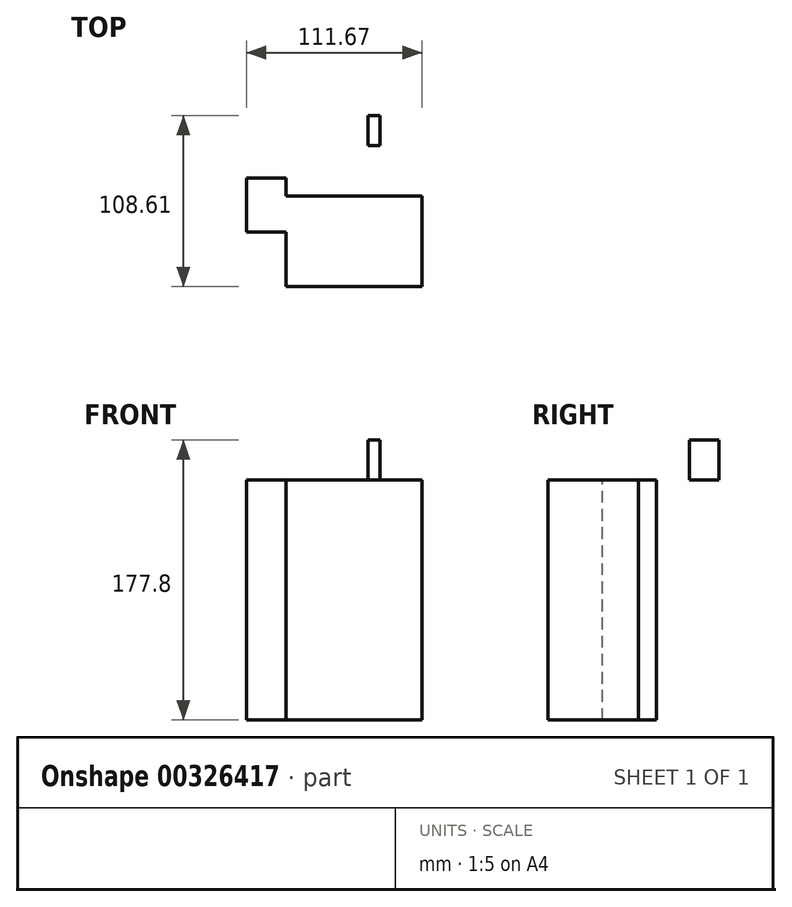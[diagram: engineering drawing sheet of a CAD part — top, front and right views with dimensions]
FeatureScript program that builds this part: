
annotation { "Feature Type Name" : "Feature", "Feature Type Description" : "" }
export const myFeature = defineFeature(function(context is Context, id is Id, definition is map)
    precondition{}
    {
        {
            var Q0;
            Q0=qCreatedBy(makeId("Top.planeOp"),FACE);
            var sketch = newSketch(context, id + "F0", { "sketchPlane" : qUnion([Q0])});
            skLineSegment(sketch, "E0.bottom", {"start": v(0, 73.96) * mm, "end": v(24.18, 73.96) * mm});
            skLineSegment(sketch, "E0.top", {"start": v(0, 0) * mm, "end": v(24.18, 0) * mm});
            skLineSegment(sketch, "E0.left", {"start": v(0, 73.96) * mm, "end": v(0, 0) * mm});
            skLineSegment(sketch, "E0.right", {"start": v(24.18, 73.96) * mm, "end": v(24.18, 0) * mm});
            skLineSegment(sketch, "E1.bottom", {"start": v(11.43, 51.15) * mm, "end": v(16.4, 51.15) * mm});
            skLineSegment(sketch, "E1.top", {"start": v(11.43, 54.99) * mm, "end": v(16.4, 54.99) * mm});
            skLineSegment(sketch, "E1.left", {"start": v(11.43, 51.15) * mm, "end": v(11.43, 54.99) * mm});
            skLineSegment(sketch, "E1.right", {"start": v(16.4, 51.15) * mm, "end": v(16.4, 54.99) * mm});
            skLineSegment(sketch, "E2.bottom", {"start": v(24.18, 73.96) * mm, "end": v(16.4, 73.96) * mm});
            skLineSegment(sketch, "E2.top", {"start": v(24.18, 54.99) * mm, "end": v(16.4, 54.99) * mm});
            skLineSegment(sketch, "E2.left", {"start": v(24.18, 73.96) * mm, "end": v(24.18, 54.99) * mm});
            skLineSegment(sketch, "E2.right", {"start": v(16.4, 73.96) * mm, "end": v(16.4, 54.99) * mm});
            skLineSegment(sketch, "E3.bottom", {"start": v(24.18, 54.99) * mm, "end": v(24.18, 54.99) * mm});
            skLineSegment(sketch, "E3.top", {"start": v(24.18, 0) * mm, "end": v(24.18, 0) * mm});
            skLineSegment(sketch, "E3.left", {"start": v(24.18, 54.99) * mm, "end": v(24.18, 0) * mm});
            skLineSegment(sketch, "E3.right", {"start": v(24.18, 54.99) * mm, "end": v(24.18, 0) * mm});
            skSolve(sketch);
        }
        {
            var Q0;
            Q0=makeQuery(id+"F0.imprint","IMPRINT",FACE,{"disambiguationData":[TD([[makeQuery(id+"F0.imprint","IMPRINT",EDGE,{"derivedFrom":sQuery(id+"F0.wireOp",EDGE,"E0.bottom")}),-1.0]])]});
            extrude(context, id + "F1", {"entities" : qUnion([Q0]), "depth" : 25.4 * mm});
        }
        {
            var Q0;
            Q0=qCreatedBy(makeId("Top.planeOp"),FACE);
            var sketch = newSketch(context, id + "F2", { "sketchPlane" : qUnion([Q0])});
            skLineSegment(sketch, "E4.bottom", {"start": v(-35.48, -34.65) * mm, "end": v(50.83, -34.65) * mm});
            skLineSegment(sketch, "E4.top", {"start": v(-35.48, 22.82) * mm, "end": v(50.83, 22.82) * mm});
            skLineSegment(sketch, "E4.left", {"start": v(-35.48, -34.65) * mm, "end": v(-35.48, 22.82) * mm});
            skLineSegment(sketch, "E4.right", {"start": v(50.83, -34.65) * mm, "end": v(50.83, 22.82) * mm});
            skLineSegment(sketch, "E5.bottom", {"start": v(-60.84, 34.31) * mm, "end": v(-35.48, 34.31) * mm});
            skLineSegment(sketch, "E5.top", {"start": v(-60.84, 0) * mm, "end": v(-35.48, 0) * mm});
            skLineSegment(sketch, "E5.left", {"start": v(-60.84, 34.31) * mm, "end": v(-60.84, 0) * mm});
            skLineSegment(sketch, "E5.right", {"start": v(-35.48, 34.31) * mm, "end": v(-35.48, 0) * mm});
            skLineSegment(sketch, "E6.top", {"start": v(-60.84, -34.65) * mm, "end": v(-35.48, -34.65) * mm});
            skLineSegment(sketch, "E6.left", {"start": v(-60.84, 0) * mm, "end": v(-60.84, -34.65) * mm});
            skLineSegment(sketch, "E6.right", {"start": v(-35.48, 0) * mm, "end": v(-35.48, -34.65) * mm});
            skSolve(sketch);
        }
        {
            var Q0;
            Q0=makeQuery(id+"F2.imprint","IMPRINT",FACE,{"disambiguationData":[TD([[makeQuery(id+"F2.imprint","IMPRINT",EDGE,{"derivedFrom":sQuery(id+"F2.wireOp",EDGE,"E4.bottom")}),1.0]])]});
            var Q1;
            {var subQ3=sQuery(id+"F2.wireOp",EDGE,"E5.bottom");Q1=makeQuery(id+"F2.imprint","IMPRINT",FACE,{"disambiguationData":[TD([[makeQuery(id+"F2.imprint","IMPRINT",EDGE,{"derivedFrom":subQ3}),-1.0]])]});}
            extrude(context, id + "F3", {"entities" : qUnion([Q0, Q1]), "oppositeDirection" : true, "depth" : 152.4 * mm});
        }
    });
